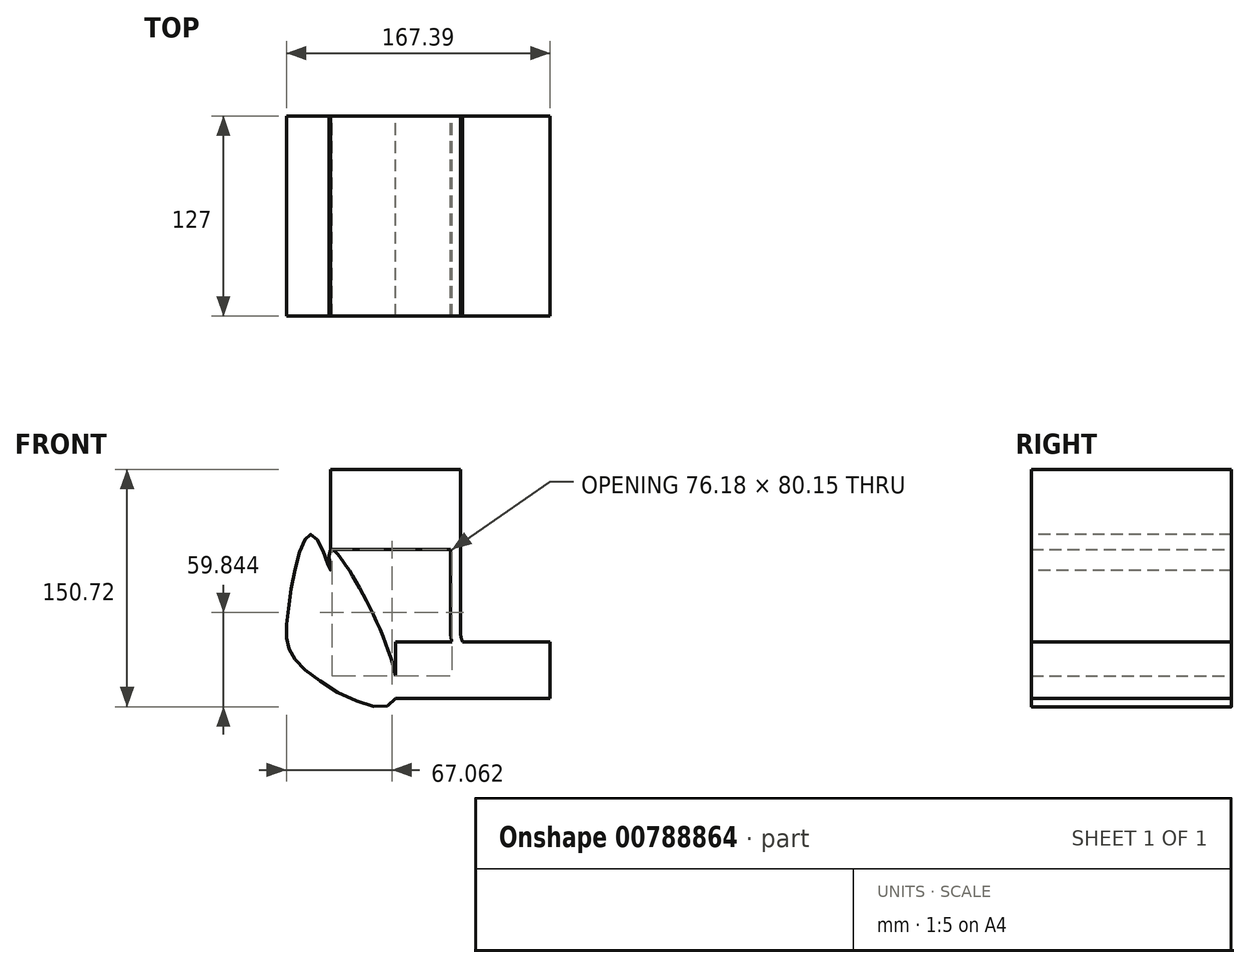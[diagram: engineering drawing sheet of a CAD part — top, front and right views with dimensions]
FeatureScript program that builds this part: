
annotation { "Feature Type Name" : "Feature", "Feature Type Description" : "" }
export const myFeature = defineFeature(function(context is Context, id is Id, definition is map)
    precondition{}
    {
        {
            var Q0;
            Q0=qCreatedBy(makeId("Front.planeOp"),FACE);
            var sketch = newSketch(context, id + "F0", { "sketchPlane" : qUnion([Q0])});
            skLineSegment(sketch, "E0.bottom", {"start": v(41.27, 25.4) * mm, "end": v(-41.28, 25.4) * mm});
            skLineSegment(sketch, "E0.top", {"start": v(41.28, -25.4) * mm, "end": v(-41.27, -25.4) * mm});
            skLineSegment(sketch, "E0.left", {"start": v(41.27, 25.4) * mm, "end": v(41.28, -25.4) * mm});
            skLineSegment(sketch, "E0.right", {"start": v(-41.28, 25.4) * mm, "end": v(-41.27, -25.4) * mm});
            skPoint(sketch, "E0.middle", {"position": v(0, 0) * mm});
            skLineSegment(sketch, "E1.bottom", {"start": v(0, -119.83) * mm, "end": v(98.07, -119.83) * mm});
            skLineSegment(sketch, "E1.top", {"start": v(0, -84.05) * mm, "end": v(98.07, -84.05) * mm});
            skLineSegment(sketch, "E1.left", {"start": v(0, -119.83) * mm, "end": v(0, -84.05) * mm});
            skLineSegment(sketch, "E1.right", {"start": v(98.07, -119.83) * mm, "end": v(98.07, -84.05) * mm});
            skLineSegment(sketch, "E2", {"start": v(41.28, -25.4) * mm, "end": v(41.28, -77.96) * mm});
            skArc(sketch, "E3", {"start": v(41.28, -77.96) * mm, "mid": v(55.84, -92.52) * mm, "end": v(70.4, -77.96) * mm});
            skLineSegment(sketch, "E4", {"start": v(70.4, -77.96) * mm, "end": v(70.4, -37.89) * mm});
            skArc(sketch, "E5.0", {"start": v(34.93, -77.96) * mm, "mid": v(55.84, -98.87) * mm, "end": v(76.75, -77.96) * mm});
            skLineSegment(sketch, "E6.0", {"start": v(34.93, -25.4) * mm, "end": v(34.93, -77.96) * mm});
            skLineSegment(sketch, "E7.0", {"start": v(76.75, -77.96) * mm, "end": v(76.75, -37.89) * mm});
            skPoint(sketch, "E8.2.internal.snap0", {"position": v(0, -101.94) * mm});
            skFitSpline(sketch, "E8", {"points": [v(-41.27, -25.4) * mm, v(0, -119.83) * mm, v(-57.16, -101.94) * mm, v(-68.4, -65.57) * mm, v(-52.66, -16.1) * mm, v(-41.27, -38.58) * mm, v(-41.27, -25.4) * mm]});
            skSolve(sketch);
        }
        {
            var Q0;
            Q0 = qSketchRegion(id + "F0", true);
            extrude(context, id + "F1", {"entities" : qUnion([Q0]), "endBound" : BoundingType.SYMMETRIC, "depth" : 127 * mm, "offsetDistance" : 25.4 * mm});
        }
    });
